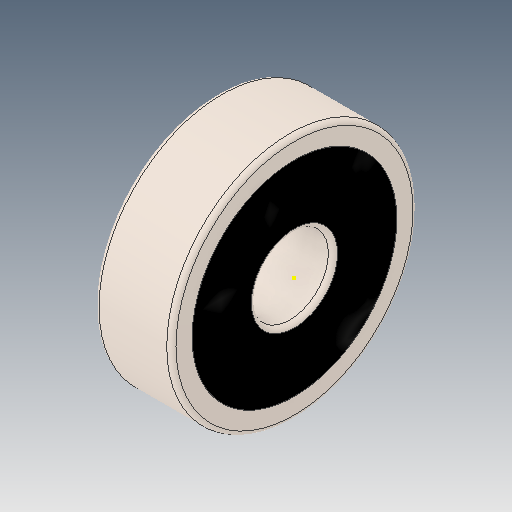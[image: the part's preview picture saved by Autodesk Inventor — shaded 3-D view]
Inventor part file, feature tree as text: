
AUTODESK INVENTOR PART (.ipt)
format: ipt  version: 2017 (Build 210142000, 142)  size: 2,300,928 bytes
history: imported  units: mm
features: other x22, sketch x3, imported_body x1
ambient origin geometry x8: Origin, YZ Plane, XZ Plane, XY Plane, X Axis, Y Axis, Z Axis, Center Point
bodies: Solid1 (imported_parasolid), Solid2 (imported_parasolid), Solid3 (imported_parasolid), Solid4 (imported_parasolid), Solid5 (imported_parasolid), Solid6 (imported_parasolid), Solid7 (imported_parasolid), Solid8 (imported_parasolid), Solid9 (imported_parasolid), Solid10 (imported_parasolid), Solid11 (imported_parasolid), Solid12 (imported_parasolid), Solid13 (imported_parasolid), Solid14 (imported_parasolid), Solid15 (imported_parasolid), Solid16 (imported_parasolid), Solid17 (imported_parasolid), Solid18 (imported_parasolid), Solid19 (imported_parasolid), Solid20 (imported_parasolid)
feature tree (26):
  other  "SKF 625.ipt"
  other  "Solid1::SKF 625.ipt"
  other  "Solid2::SKF 625.ipt"
  other  "Solid3::SKF 625.ipt"
  other  "Solid4::SKF 625.ipt"
  other  "Solid5::SKF 625.ipt"
  other  "Solid6::SKF 625.ipt"
  other  "Solid7::SKF 625.ipt"
  other  "Solid8::SKF 625.ipt"
  other  "Solid9::SKF 625.ipt"
  other  "Solid10::SKF 625.ipt"
  other  "Solid11::SKF 625.ipt"
  other  "Solid12::SKF 625.ipt"
  other  "Solid13::SKF 625.ipt"
  other  "Solid14::SKF 625.ipt"
  other  "Solid15::SKF 625.ipt"
  other  "Solid16::SKF 625.ipt"
  other  "Solid17::SKF 625.ipt"
  other  "Solid18::SKF 625.ipt"
  other  "Solid19::SKF 625.ipt"
  other  "Solid20::SKF 625.ipt"
  other  "TaggingFeature1"
  sketch  "Sketch1"  dims[d0=10.0mm]
  sketch  "Sketch2"
  sketch  "Sketch3"
  imported_body  NMx_Import_Brep_tag  [imported B-rep: ~49 faces, bbox_mm=None]
